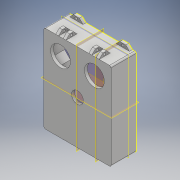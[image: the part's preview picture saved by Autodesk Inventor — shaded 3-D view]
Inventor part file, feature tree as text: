
AUTODESK INVENTOR PART (.ipt)
format: ipt  version: 2017 (Build 210142000, 142)  size: 374,784 bytes
history: native  units: mm
features: sketch x7, extrude x6, plane x4, mirror x2, fillet x1, pattern_linear x1, projected_geometry x1
ambient origin geometry x8: Origin, YZ Plane, XZ Plane, XY Plane, X Axis, Y Axis, Z Axis, Center Point
bodies: Solid1 (feature_tree)
feature tree (22):
  extrude  "Extrusion1"  Depth=100.0mm
  extrude  "Extrusion2"  Depth=4.0mm
  extrude  "Extrusion3"  Depth=4.0mm
  fillet  "Fillet1"  Radius=43.0mm
  plane  "Work Plane1"
  extrude  "Extrusion4"  Depth=43.0mm
  extrude  "Extrusion5"  Depth=23.5mm
  sketch  "Sketch9"  dims[d12=5.0mm d13=13.0mm]
  plane  "Work Plane2"
  extrude  "Extrusion6"  Depth=13.0mm
  plane  "Work Plane3"
  plane  "Work Plane5"
  pattern_linear  "Rectangular Pattern1"  Spacing1=27.0mm  [1 undecoded]
  mirror  "Mirror3"
  mirror  "Mirror4"
  sketch  "Sketch1"  dims[d0=47.0mm d1=100.0mm]
  sketch  "Sketch3"  dims[d2=3.2mm d3=4.0mm]
  sketch  "Sketch4"  dims[d4=4.0mm d5=4.0mm d6=43.0mm]
  sketch  "Sketch6"  dims[d7=3.2mm d8=43.0mm]
  sketch  "Sketch8"  dims[d9=96.0mm d11=23.5mm]
  projected_geometry  "Projected Loop1"
  sketch  "Sketch10"  dims[d14=18.0mm d15=27.0mm d16=23.0mm d17=27.0mm d18=16.0mm d19=50.0mm d20=5.0mm d21=5.0mm d22=5.0mm d23=5.0mm d24=4.0mm d25=0.0mm d30=4.0mm d31=4.0mm d32=4.0mm d33=4.0mm d34=34.0mm d35=0.0mm d36=1.0mm d37=2.0mm d38=1.0mm d39=2.0mm d40=1.0mm d41=2.0mm d42=1.0mm d43=2.0mm d44=4.0mm d45=0.0mm d46=2.0mm d47=20.0mm d48=47.0mm d49=100.0mm d50=3.2mm d51=4.0mm d52=4.0mm d53=3.2mm d55=20.0mm d57=3.2mm d58=3.2mm d61=4.0mm d62=4.0mm d63=45.0deg d64=45.0deg d65=20.0mm d66=90.0deg d67=8.0mm d68=135.0deg d69=135.0deg d70=3.2mm d71=3.2mm d72=4.0mm d73=0.0mm d74=8.0mm d77=8.0mm d80=135.0deg d81=45.0deg d82=135.0deg d83=45.0deg d84=3.2mm d85=3.2mm d86=8.0mm d89=8.0mm d91=10.0mm d92=10.0mm d93=45.0deg d94=135.0deg d95=135.0deg d96=3.2mm d97=3.2mm d98=4.0mm d99=0.0mm d100=12.0mm d101=0.0mm d102=4.0mm d103=12.0mm d104=-20.0mm d106=5.0mm d108=3.2mm d109=4.0mm d110=0.0mm d111=-45.5mm d112=-59.25mm d113=20.0mm d115=10.0mm d116=10.0mm d118=10.0mm]
note: 1 required parameter value undecoded (feature->parameter linkage not recoverable at this tier; creation-order binding heuristic only, values carry confidence <= 0.55)
